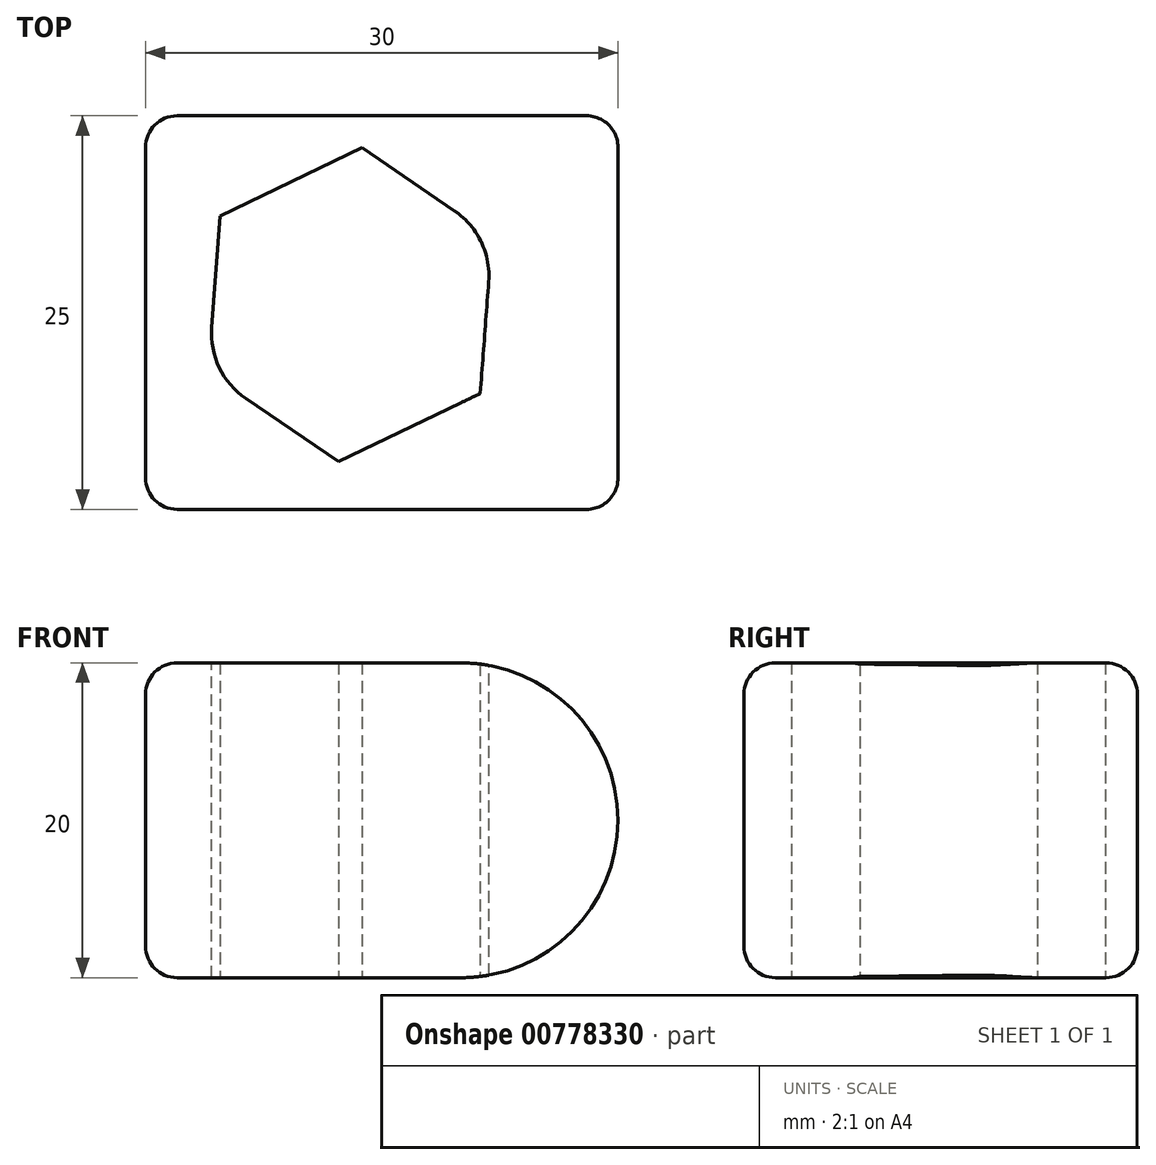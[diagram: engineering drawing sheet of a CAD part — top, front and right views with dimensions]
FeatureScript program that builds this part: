
annotation { "Feature Type Name" : "Feature", "Feature Type Description" : "" }
export const myFeature = defineFeature(function(context is Context, id is Id, definition is map)
    precondition{}
    {
        {
            var Q0;
            Q0=qCreatedBy(makeId("Front.planeOp"),FACE);
            var sketch = newSketch(context, id + "F0", { "sketchPlane" : qUnion([Q0])});
            skLineSegment(sketch, "E0.bottom", {"start": v(-10, 10) * mm, "end": v(10, 10) * mm});
            skLineSegment(sketch, "E0.top", {"start": v(-10, -10) * mm, "end": v(10, -10) * mm});
            skLineSegment(sketch, "E0.left", {"start": v(-10, 10) * mm, "end": v(-10, -10) * mm});
            skArc(sketch, "E1", {"start": v(10, 10) * mm, "mid": v(20, 0) * mm, "end": v(10, -10) * mm});
            skSolve(sketch);
        }
        {
            var Q0;
            Q0=makeQuery(id+"F0.imprint","IMPRINT",FACE,{"disambiguationData":[TD([[makeQuery(id+"F0.imprint","IMPRINT",EDGE,{"derivedFrom":sQuery(id+"F0.wireOp",EDGE,"E0.bottom")}),-1.0]])]});
            extrude(context, id + "F1", {"entities" : qUnion([Q0]), "depth" : 25 * mm, "offsetDistance" : 25 * mm});
        }
        {
            var Q0;
            Q0=qCreatedBy(makeId("Top.planeOp"),FACE);
            var sketch = newSketch(context, id + "F2", { "sketchPlane" : qUnion([Q0])});
            skCircle(sketch, "E2.cCircle", {"center": v(3, -12) * mm, "radius": 10 * mm, "construction": true});
            skLineSegment(sketch, "E2.0", {"start": v(11.25, -17.64) * mm, "end": v(2.24, -21.97) * mm});
            skLineSegment(sketch, "E2.1", {"start": v(2.24, -21.97) * mm, "end": v(-6.02, -16.33) * mm});
            skLineSegment(sketch, "E2.2", {"start": v(-6.02, -16.33) * mm, "end": v(-5.27, -6.36) * mm});
            skLineSegment(sketch, "E2.3", {"start": v(-5.27, -6.36) * mm, "end": v(3.75, -2.03) * mm});
            skLineSegment(sketch, "E2.4", {"start": v(3.75, -2.03) * mm, "end": v(12, -7.67) * mm});
            skLineSegment(sketch, "E2.5", {"start": v(12, -7.67) * mm, "end": v(11.25, -17.64) * mm});
            skSolve(sketch);
        }
        {
            var Q0;
            Q0=makeQuery(id+"F2.imprint","IMPRINT",FACE,{"disambiguationData":[TD([[makeQuery(id+"F2.imprint","IMPRINT",EDGE,{"derivedFrom":sQuery(id+"F2.wireOp",EDGE,"E2.0")}),-1.0]])]});
            var Q1;
            Q1=sQuery(id+"F2.wireOp",EDGE,"E2.3");
            var Q2;
            Q2=sQuery(id+"F2.wireOp",EDGE,"E2.1");
            var Q3;
            Q3=sQuery(id+"F2.wireOp",EDGE,"E2.2");
            var Q4;
            Q4=sQuery(id+"F2.wireOp",EDGE,"E2.4");
            var Q5;
            Q5=sQuery(id+"F2.wireOp",EDGE,"E2.5");
            var Q6;
            Q6=sQuery(id+"F2.wireOp",EDGE,"E2.0");
            extrude(context, id + "F3", {"entities" : qUnion([Q0]), "operationType" : NewBodyOperationType.REMOVE, "surfaceEntities" : qUnion([Q1, Q2, Q3, Q4, Q5, Q6]), "endBound" : BoundingType.SYMMETRIC, "depth" : 25 * mm, "offsetDistance" : 25 * mm});
        }
        {
            var Q0;
            Q0=makeQuery(id+"F1.opExtrude","CAP_EDGE",EDGE,{"disambiguationData":[OSD([sQuery(id+"F0.wireOp",EDGE,"E1")])],"isStart":true});
            var Q1;
            Q1=makeQuery(id+"F1.opExtrude","CAP_EDGE",EDGE,{"disambiguationData":[OSD([sQuery(id+"F0.wireOp",EDGE,"E1")])],"isStart":false});
            var Q2;
            Q2=makeQuery(id+"F1.opExtrude","CAP_EDGE",EDGE,{"disambiguationData":[OSD([sQuery(id+"F0.wireOp",EDGE,"E0.left")])],"isStart":false});
            var Q3;
            Q3=makeQuery(id+"F1.opExtrude","SWEPT_EDGE",EDGE,{"disambiguationData":[OSD([sQuery(id+"F0.wireOp",EDGE,"E0.top"),sQuery(id+"F0.wireOp",EDGE,"E0.left")])]});
            var Q4;
            Q4=makeQuery(id+"F1.opExtrude","SWEPT_EDGE",EDGE,{"disambiguationData":[OSD([sQuery(id+"F0.wireOp",EDGE,"E0.bottom"),sQuery(id+"F0.wireOp",EDGE,"E0.left")])]});
            var Q5;
            Q5=makeQuery(id+"F1.opExtrude","CAP_EDGE",EDGE,{"disambiguationData":[OSD([sQuery(id+"F0.wireOp",EDGE,"E0.left")])],"isStart":true});
            fillet(context, id + "F4", {"entities" : qUnion([Q0, Q1, Q2, Q3, Q4, Q5]), "radius" : 2 * mm, "tangentPropagation" : true, "allowEdgeOverflow" : false});
        }
        {
            var Q0;
            Q0=makeQuery(id+"F3.boolean.opBoolean","COPY",EDGE,{"derivedFrom":makeQuery(id+"F3.opExtrude","SWEPT_EDGE",EDGE,{"disambiguationData":[OSD([sQuery(id+"F2.wireOp",EDGE,"E2.1"),sQuery(id+"F2.wireOp",EDGE,"E2.2")])]})});
            var Q1;
            Q1=makeQuery(id+"F3.boolean.opBoolean","COPY",EDGE,{"derivedFrom":makeQuery(id+"F3.opExtrude","SWEPT_EDGE",EDGE,{"disambiguationData":[OSD([sQuery(id+"F2.wireOp",EDGE,"E2.4"),sQuery(id+"F2.wireOp",EDGE,"E2.5")])]})});
            fillet(context, id + "F5", {"entities" : qUnion([Q0, Q1]), "radius" : 5 * mm, "tangentPropagation" : true, "allowEdgeOverflow" : false});
        }
    });
